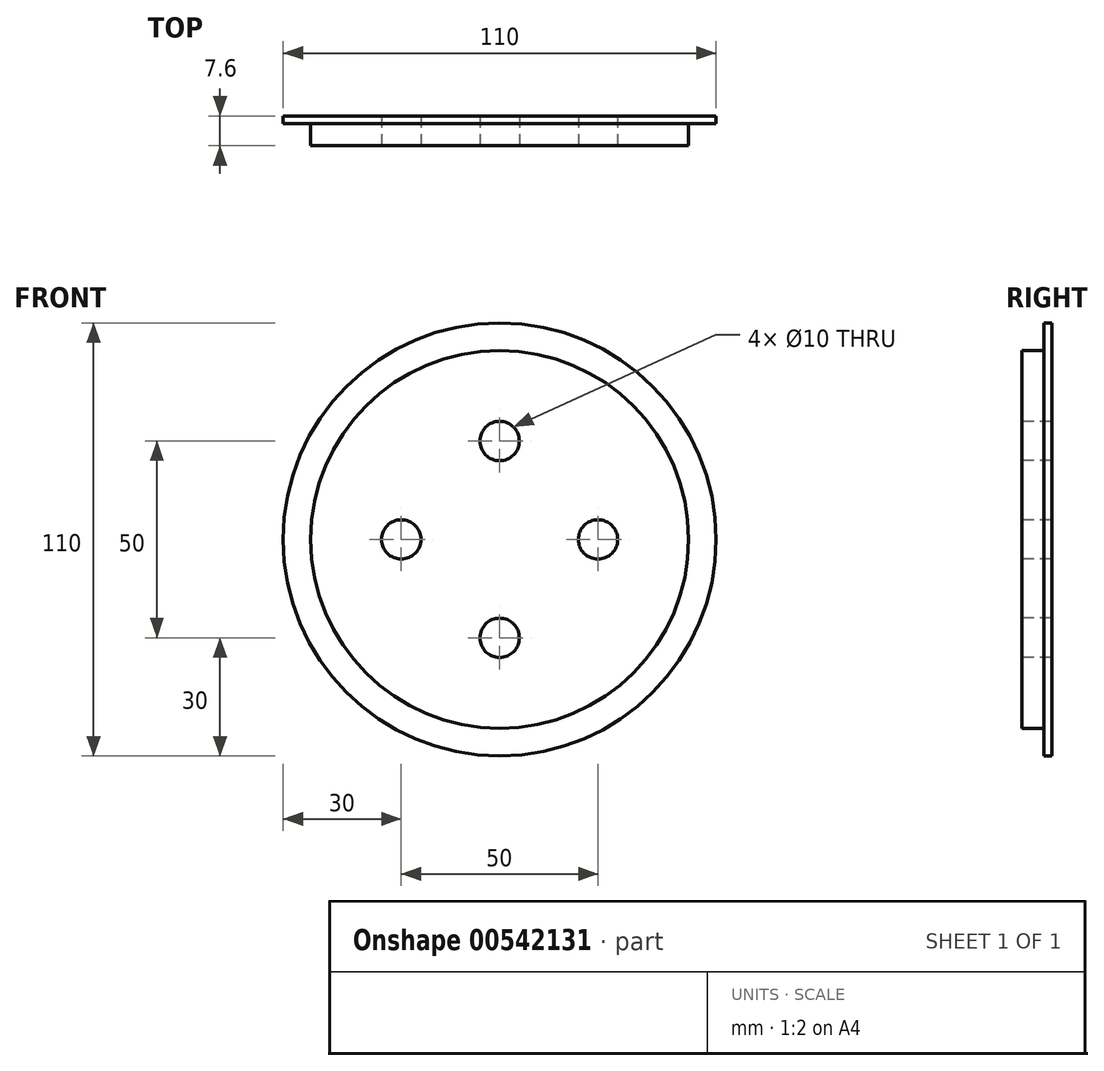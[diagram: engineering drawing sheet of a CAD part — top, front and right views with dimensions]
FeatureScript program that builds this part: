
annotation { "Feature Type Name" : "Feature", "Feature Type Description" : "" }
export const myFeature = defineFeature(function(context is Context, id is Id, definition is map)
    precondition{}
    {
        {
            var Q0;
            Q0=qCreatedBy(makeId("Front.planeOp"),FACE);
            var sketch = newSketch(context, id + "F0", { "sketchPlane" : qUnion([Q0])});
            skCircle(sketch, "E0", {"center": v(0, 0) * mm, "radius": 55 * mm});
            skSolve(sketch);
        }
        {
            var Q0;
            Q0 = qSketchRegion(id + "F0", true);
            extrude(context, id + "F1", {"entities" : qUnion([Q0]), "depth" : 2 * mm, "offsetDistance" : 25 * mm});
        }
        {
            var Q0;
            Q0=makeQuery(id+"F1.opExtrude","CAP_FACE",FACE,{"disambiguationData":[OSD([sQuery(id+"F0.wireOp",EDGE,"E0")])],"isStart":false});
            var sketch = newSketch(context, id + "F2", { "sketchPlane" : qUnion([Q0])});
            skCircle(sketch, "E1", {"center": v(0, 0) * mm, "radius": 48 * mm});
            skSolve(sketch);
        }
        {
            var Q0;
            Q0 = qSketchRegion(id + "F2", true);
            extrude(context, id + "F3", {"entities" : qUnion([Q0]), "operationType" : NewBodyOperationType.ADD, "depth" : 5.6 * mm, "offsetDistance" : 25 * mm});
        }
        {
            var Q0;
            Q0=makeQuery(id+"F3.opExtrude","CAP_FACE",FACE,{"disambiguationData":[OSD([sQuery(id+"F2.wireOp",EDGE,"E1")])],"isStart":false});
            var sketch = newSketch(context, id + "F4", { "sketchPlane" : qUnion([Q0])});
            skCircle(sketch, "E2", {"center": v(0, 0) * mm, "radius": 25 * mm, "construction": true});
            skCircle(sketch, "E3", {"center": v(0, 25) * mm, "radius": 5.12 * mm});
            skCircle(sketch, "E4", {"center": v(25, 0) * mm, "radius": 5.51 * mm});
            skCircle(sketch, "E5", {"center": v(0, -25) * mm, "radius": 5.17 * mm});
            skCircle(sketch, "E6", {"center": v(-25, 0) * mm, "radius": 5.65 * mm});
            skSolve(sketch);
        }
        {
            var Q0;
            Q0=sQuery(id+"F4.wireOp",VERTEX,"E6.center");
            var Q1;
            Q1=sQuery(id+"F4.wireOp",VERTEX,"E3.center");
            var Q2;
            Q2=sQuery(id+"F4.wireOp",VERTEX,"E4.center");
            var Q3;
            Q3=sQuery(id+"F4.wireOp",VERTEX,"E5.center");
            var Q4;
            Q4=makeQuery(id+"F1.opExtrude","SWEPT_BODY",BODY,{"disambiguationData":[OSD([sQuery(id+"F0.wireOp",EDGE,"E0")])]});
            hole(context, id + "F5", {"style" : HoleStyle.SIMPLE, "endStyle" : HoleEndStyle.THROUGH, "holeDiameter" : 10 * mm, "isTappedThrough" : true, "tappedDepth" : 12 * mm, "tapClearance" : 3, "locations" : qUnion([Q0, Q1, Q2, Q3]), "scope" : qUnion([Q4])});
        }
    });
